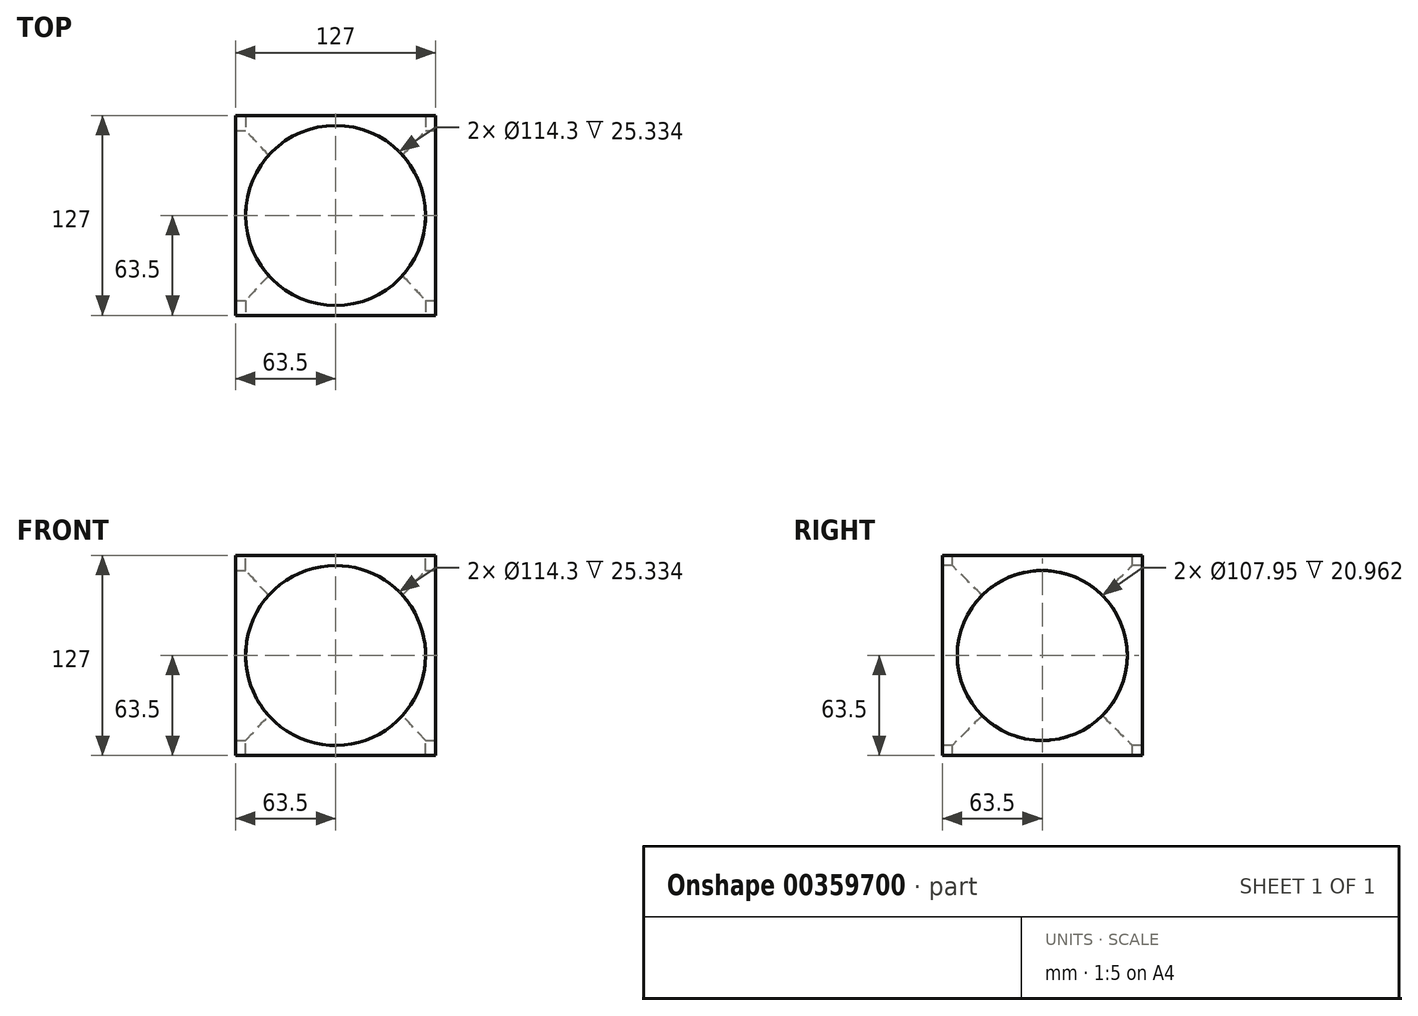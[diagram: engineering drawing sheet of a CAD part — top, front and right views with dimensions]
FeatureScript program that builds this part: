
annotation { "Feature Type Name" : "Feature", "Feature Type Description" : "" }
export const myFeature = defineFeature(function(context is Context, id is Id, definition is map)
    precondition{}
    {
        {
            var Q0;
            Q0=qCreatedBy(makeId("Right.planeOp"),FACE);
            var sketch = newSketch(context, id + "F0", { "sketchPlane" : qUnion([Q0])});
            skLineSegment(sketch, "E0.bottom", {"start": v(-63.5, 63.5) * mm, "end": v(63.5, 63.5) * mm});
            skLineSegment(sketch, "E0.top", {"start": v(-63.5, -63.5) * mm, "end": v(63.5, -63.5) * mm});
            skLineSegment(sketch, "E0.left", {"start": v(-63.5, 63.5) * mm, "end": v(-63.5, -63.5) * mm});
            skLineSegment(sketch, "E0.right", {"start": v(63.5, 63.5) * mm, "end": v(63.5, -63.5) * mm});
            skPoint(sketch, "E1", {"position": v(0, 63.5) * mm});
            skPoint(sketch, "E2", {"position": v(63.5, 0) * mm});
            skSolve(sketch);
        }
        {
            var Q0;
            Q0 = qSketchRegion(id + "F0", true);
            extrude(context, id + "F1", {"entities" : qUnion([Q0]), "endBound" : BoundingType.SYMMETRIC, "depth" : 127 * mm});
        }
        {
            var Q0;
            Q0=makeQuery(id+"F1.opExtrude","CAP_FACE",FACE,{"disambiguationData":[OSD([sQuery(id+"F0.wireOp",EDGE,"E0.bottom"),sQuery(id+"F0.wireOp",EDGE,"E0.top"),sQuery(id+"F0.wireOp",EDGE,"E0.left"),sQuery(id+"F0.wireOp",EDGE,"E0.right")])],"isStart":false});
            var sketch = newSketch(context, id + "F2", { "sketchPlane" : qUnion([Q0])});
            skCircle(sketch, "E3", {"center": v(0, 0) * mm, "radius": 53.98 * mm});
            skSolve(sketch);
        }
        {
            var Q0;
            Q0 = qSketchRegion(id + "F2", true);
            var Q1;
            Q1=makeQuery(id+"F1.opExtrude","CAP_FACE",FACE,{"disambiguationData":[OSD([sQuery(id+"F0.wireOp",EDGE,"E0.bottom"),sQuery(id+"F0.wireOp",EDGE,"E0.top"),sQuery(id+"F0.wireOp",EDGE,"E0.left"),sQuery(id+"F0.wireOp",EDGE,"E0.right")])],"isStart":true});
            extrude(context, id + "F3", {"entities" : qUnion([Q0]), "operationType" : NewBodyOperationType.REMOVE, "endBound" : BoundingType.UP_TO_SURFACE, "oppositeDirection" : true, "endBoundEntityFace" : qUnion([Q1]), "depth" : 25.4 * mm});
        }
        {
            var Q0;
            Q0=makeQuery(id+"F1.opExtrude","SWEPT_FACE",FACE,{"disambiguationData":[OSD([sQuery(id+"F0.wireOp",EDGE,"E0.left")])]});
            var sketch = newSketch(context, id + "F4", { "sketchPlane" : qUnion([Q0])});
            skCircle(sketch, "E4", {"center": v(0, 0) * mm, "radius": 57.15 * mm});
            skSolve(sketch);
        }
        {
            var Q0;
            Q0 = qSketchRegion(id + "F4", true);
            extrude(context, id + "F5", {"entities" : qUnion([Q0]), "operationType" : NewBodyOperationType.REMOVE, "endBound" : BoundingType.SYMMETRIC, "oppositeDirection" : true, "depth" : 263.14 * mm});
        }
        {
            var Q0;
            Q0=makeQuery(id+"F1.opExtrude","SWEPT_FACE",FACE,{"disambiguationData":[OSD([sQuery(id+"F0.wireOp",EDGE,"E0.bottom")])]});
            var sketch = newSketch(context, id + "F6", { "sketchPlane" : qUnion([Q0])});
            skCircle(sketch, "E5", {"center": v(0, 0) * mm, "radius": 57.15 * mm});
            skSolve(sketch);
        }
        {
            var Q0;
            Q0 = qSketchRegion(id + "F6", true);
            extrude(context, id + "F7", {"entities" : qUnion([Q0]), "operationType" : NewBodyOperationType.REMOVE, "endBound" : BoundingType.SYMMETRIC, "oppositeDirection" : true, "depth" : 287.02 * mm});
        }
    });
